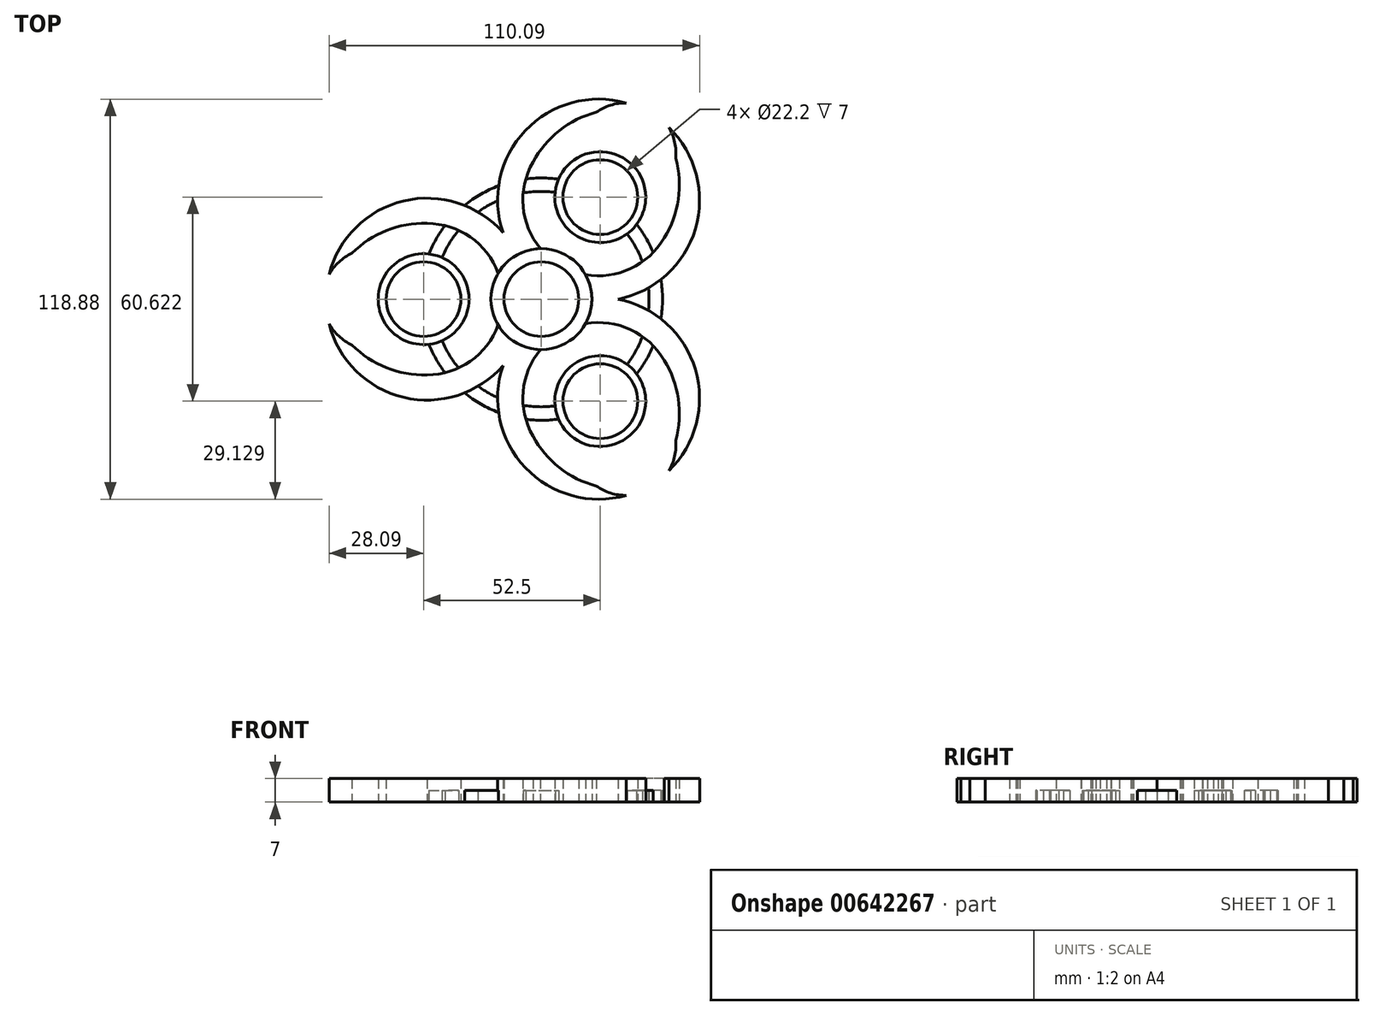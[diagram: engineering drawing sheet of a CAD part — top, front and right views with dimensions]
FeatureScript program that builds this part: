
annotation { "Feature Type Name" : "Feature", "Feature Type Description" : "" }
export const myFeature = defineFeature(function(context is Context, id is Id, definition is map)
    precondition{}
    {
        {
            var Q0;
            Q0=qCreatedBy(makeId("Top.planeOp"),FACE);
            var sketch = newSketch(context, id + "F0", { "sketchPlane" : qUnion([Q0])});
            skCircle(sketch, "E0", {"center": v(0, 0) * mm, "radius": 11.1 * mm});
            skCircle(sketch, "E1", {"center": v(0, 0) * mm, "radius": 15 * mm});
            skLineSegment(sketch, "E2", {"start": v(0, 0) * mm, "end": v(-35, 0) * mm, "construction": true});
            skCircle(sketch, "E3", {"center": v(-35, 0) * mm, "radius": 11.1 * mm});
            skCircle(sketch, "E4", {"center": v(-35, 0) * mm, "radius": 13.5 * mm});
            skCircle(sketch, "E5.1.0", {"center": v(17.5, -30.31) * mm, "radius": 11.1 * mm});
            skCircle(sketch, "E5.1.1", {"center": v(17.5, -30.31) * mm, "radius": 13.5 * mm});
            skCircle(sketch, "E5.2.0", {"center": v(17.5, 30.31) * mm, "radius": 11.1 * mm});
            skCircle(sketch, "E5.2.1", {"center": v(17.5, 30.31) * mm, "radius": 13.5 * mm});
            skSolve(sketch);
        }
        {
            var Q0;
            Q0=qCreatedBy(makeId("Top.planeOp"),FACE);
            var sketch = newSketch(context, id + "F1", { "sketchPlane" : qUnion([Q0])});
            skLineSegment(sketch, "E6", {"start": v(0, 0) * mm, "end": v(-34, 0) * mm, "construction": true});
            skArc(sketch, "E7", {"start": v(-34, -22.5) * mm, "mid": v(-11.5, 0) * mm, "end": v(-34, 22.5) * mm});
            skCircle(sketch, "E8", {"center": v(-34, 0) * mm, "radius": 30 * mm});
            skLineSegment(sketch, "E9", {"start": v(-34, 0) * mm, "end": v(-34, 30) * mm, "construction": true});
            skLineSegment(sketch, "E10", {"start": v(-34, 0) * mm, "end": v(-34, -30) * mm, "construction": true});
            skLineSegment(sketch, "E11", {"start": v(-34, 0) * mm, "end": v(-64, 0) * mm, "construction": true});
            skArc(sketch, "E12", {"start": v(-34, 22.5) * mm, "mid": v(-52.95, 16.52) * mm, "end": v(-64, 0) * mm});
            skArc(sketch, "E13.MirrorCS", {"start": v(-34, -22.5) * mm, "mid": v(-52.95, -16.52) * mm, "end": v(-64, 0) * mm});
            skPoint(sketch, "E14.center", {"position": v(0, 0) * mm});
            skCircle(sketch, "E15.0.0", {"center": v(0, 0) * mm, "radius": 15 * mm});
            skCircle(sketch, "E16.0.0", {"center": v(-35, 0) * mm, "radius": 13.5 * mm, "construction": true});
            skCircle(sketch, "E17.0.0", {"center": v(17.5, 30.31) * mm, "radius": 13.5 * mm, "construction": true});
            skCircle(sketch, "E18.0.0", {"center": v(17.5, -30.31) * mm, "radius": 13.5 * mm, "construction": true});
            skCircle(sketch, "E19.0", {"center": v(0, 0) * mm, "radius": 11.1 * mm});
            skCircle(sketch, "E20", {"center": v(-50, 0) * mm, "radius": 15 * mm});
            skArc(sketch, "E21.1.0", {"start": v(36.49, -18.2) * mm, "mid": v(5.75, -9.96) * mm, "end": v(-2.49, -40.7) * mm});
            skArc(sketch, "E21.1.1", {"start": v(36.49, -18.2) * mm, "mid": v(40.78, -37.6) * mm, "end": v(32, -55.43) * mm});
            skArc(sketch, "E21.1.2", {"start": v(-2.49, -40.7) * mm, "mid": v(12.17, -54.11) * mm, "end": v(32, -55.43) * mm});
            skCircle(sketch, "E21.1.3", {"center": v(17, -29.44) * mm, "radius": 30 * mm});
            skCircle(sketch, "E21.1.4", {"center": v(25, -43.3) * mm, "radius": 15 * mm});
            skArc(sketch, "E21.2.0", {"start": v(-2.49, 40.7) * mm, "mid": v(5.75, 9.96) * mm, "end": v(36.49, 18.2) * mm});
            skArc(sketch, "E21.2.1", {"start": v(-2.49, 40.7) * mm, "mid": v(12.17, 54.11) * mm, "end": v(32, 55.43) * mm});
            skArc(sketch, "E21.2.2", {"start": v(36.49, 18.2) * mm, "mid": v(40.78, 37.6) * mm, "end": v(32, 55.43) * mm});
            skCircle(sketch, "E21.2.3", {"center": v(17, 29.44) * mm, "radius": 30 * mm});
            skCircle(sketch, "E21.2.4", {"center": v(25, 43.3) * mm, "radius": 15 * mm});
            skSolve(sketch);
        }
        {
            var Q0;
            Q0=makeQuery(id+"F0.imprint","IMPRINT",FACE,{"disambiguationData":[TD([[makeQuery(id+"F0.imprint","IMPRINT",EDGE,{"derivedFrom":sQuery(id+"F0.wireOp",EDGE,"E0")}),-1.0]])]});
            var Q1;
            {var subQ0=sQuery(id+"F1.wireOp",EDGE,"E12");var subQ1=sQuery(id+"F1.wireOp",EDGE,"E7");var subQ2=makeQuery(id+"F1.imprint","INTERSECT",VERTEX,{"derivedFrom":[subQ1,subQ0]});Q1=makeQuery(id+"F1.imprint","IMPRINT",FACE,{"disambiguationData":[TD([[makeQuery(id+"F1.imprint","IMPRINT",EDGE,{"disambiguationData":[TD([[subQ2,1.0]])],"derivedFrom":subQ1}),-1.0]])]});}
            var Q2;
            {var subQ7=sQuery(id+"F1.wireOp",EDGE,"E8");var subQ9=sQuery(id+"F1.wireOp",EDGE,"E21.2.3");var subQ10=makeQuery(id+"F1.imprint","INTERSECT",VERTEX,{"disambiguationData":[OD(0.0)],"derivedFrom":[subQ7,subQ9]});Q2=makeQuery(id+"F1.imprint","IMPRINT",FACE,{"disambiguationData":[TD([[makeQuery(id+"F1.imprint","IMPRINT",EDGE,{"disambiguationData":[TD([[subQ10,1.0]])],"derivedFrom":subQ7}),-1.0]])]});}
            var Q3;
            {var subQ1=sQuery(id+"F1.wireOp",EDGE,"E21.2.0");var subQ5=sQuery(id+"F1.wireOp",EDGE,"E15.0.0");var subQ6=makeQuery(id+"F1.imprint","INTERSECT",VERTEX,{"disambiguationData":[OD(0.0)],"derivedFrom":[subQ5,subQ1]});Q3=makeQuery(id+"F1.imprint","IMPRINT",FACE,{"disambiguationData":[TD([[makeQuery(id+"F1.imprint","IMPRINT",EDGE,{"disambiguationData":[TD([[subQ6,1.0]])],"derivedFrom":subQ5}),-1.0]])]});}
            var Q4;
            {var subQ1=sQuery(id+"F1.wireOp",EDGE,"E21.1.0");var subQ3=sQuery(id+"F1.wireOp",EDGE,"E15.0.0");var subQ4=makeQuery(id+"F1.imprint","INTERSECT",VERTEX,{"disambiguationData":[OD(1.0)],"derivedFrom":[subQ3,subQ1]});Q4=makeQuery(id+"F1.imprint","IMPRINT",FACE,{"disambiguationData":[TD([[makeQuery(id+"F1.imprint","IMPRINT",EDGE,{"disambiguationData":[TD([[subQ4,-1.0]])],"derivedFrom":subQ3}),-1.0]])]});}
            var Q5;
            {var subQ0=sQuery(id+"F1.wireOp",EDGE,"E13.MirrorCS");var subQ1=sQuery(id+"F1.wireOp",EDGE,"E7");var subQ2=makeQuery(id+"F1.imprint","INTERSECT",VERTEX,{"derivedFrom":[subQ1,subQ0]});Q5=makeQuery(id+"F1.imprint","IMPRINT",FACE,{"disambiguationData":[TD([[makeQuery(id+"F1.imprint","IMPRINT",EDGE,{"disambiguationData":[TD([[subQ2,-1.0]])],"derivedFrom":subQ1}),-1.0]])]});}
            var Q6;
            {var subQ0=sQuery(id+"F1.wireOp",EDGE,"E21.2.3");var subQ1=sQuery(id+"F1.wireOp",EDGE,"E8");var subQ2=makeQuery(id+"F1.imprint","INTERSECT",VERTEX,{"disambiguationData":[OD(0.0)],"derivedFrom":[subQ1,subQ0]});Q6=makeQuery(id+"F1.imprint","IMPRINT",FACE,{"disambiguationData":[TD([[makeQuery(id+"F1.imprint","IMPRINT",EDGE,{"disambiguationData":[TD([[subQ2,1.0]])],"derivedFrom":subQ1}),1.0]])]});}
            var Q7;
            {var subQ0=sQuery(id+"F1.wireOp",EDGE,"E21.1.3");var subQ1=sQuery(id+"F1.wireOp",EDGE,"E15.0.0");var subQ2=makeQuery(id+"F1.imprint","INTERSECT",VERTEX,{"disambiguationData":[OD(0.0)],"derivedFrom":[subQ1,subQ0]});Q7=makeQuery(id+"F1.imprint","IMPRINT",FACE,{"disambiguationData":[TD([[makeQuery(id+"F1.imprint","IMPRINT",EDGE,{"disambiguationData":[TD([[subQ2,1.0]])],"derivedFrom":subQ1}),-1.0]])]});}
            var Q8;
            {var subQ5=sQuery(id+"F1.wireOp",EDGE,"E8");var subQ9=sQuery(id+"F1.wireOp",EDGE,"E21.1.3");var subQ10=makeQuery(id+"F1.imprint","INTERSECT",VERTEX,{"disambiguationData":[OD(0.0)],"derivedFrom":[subQ5,subQ9]});Q8=makeQuery(id+"F1.imprint","IMPRINT",FACE,{"disambiguationData":[TD([[makeQuery(id+"F1.imprint","IMPRINT",EDGE,{"disambiguationData":[TD([[subQ10,-1.0]])],"derivedFrom":subQ5}),-1.0]])]});}
            var Q9;
            {var subQ0=sQuery(id+"F1.wireOp",EDGE,"E21.1.3");var subQ1=sQuery(id+"F1.wireOp",EDGE,"E8");var subQ2=makeQuery(id+"F1.imprint","INTERSECT",VERTEX,{"disambiguationData":[OD(0.0)],"derivedFrom":[subQ1,subQ0]});Q9=makeQuery(id+"F1.imprint","IMPRINT",FACE,{"disambiguationData":[TD([[makeQuery(id+"F1.imprint","IMPRINT",EDGE,{"disambiguationData":[TD([[subQ2,-1.0]])],"derivedFrom":subQ1}),1.0]])]});}
            extrude(context, id + "F2", {"entities" : qUnion([Q0, Q1, Q2, Q3, Q4, Q5, Q6, Q7, Q8, Q9]), "depth" : 7 * mm, "offsetDistance" : 25 * mm});
        }
        {
            var Q0;
            Q0=makeQuery(id+"F0.imprint","IMPRINT",FACE,{"disambiguationData":[TD([[makeQuery(id+"F0.imprint","IMPRINT",EDGE,{"derivedFrom":sQuery(id+"F0.wireOp",EDGE,"E3")}),-1.0]])]});
            var Q1;
            Q1=makeQuery(id+"F0.imprint","IMPRINT",FACE,{"disambiguationData":[TD([[makeQuery(id+"F0.imprint","IMPRINT",EDGE,{"derivedFrom":sQuery(id+"F0.wireOp",EDGE,"E5.2.0")}),-1.0]])]});
            var Q2;
            Q2=makeQuery(id+"F0.imprint","IMPRINT",FACE,{"disambiguationData":[TD([[makeQuery(id+"F0.imprint","IMPRINT",EDGE,{"derivedFrom":sQuery(id+"F0.wireOp",EDGE,"E5.1.0")}),-1.0]])]});
            extrude(context, id + "F3", {"entities" : qUnion([Q0, Q1, Q2]), "operationType" : NewBodyOperationType.ADD, "depth" : 7 * mm, "offsetDistance" : 25 * mm});
        }
        {
            var Q0;
            Q0=qCreatedBy(makeId("Top.planeOp"),FACE);
            var sketch = newSketch(context, id + "F4", { "sketchPlane" : qUnion([Q0])});
            skArc(sketch, "E22.0", {"start": v(-34, -22.5) * mm, "mid": v(-11.5, 0) * mm, "end": v(-34, 22.5) * mm, "construction": true});
            skArc(sketch, "E23.0", {"start": v(-2.49, 40.7) * mm, "mid": v(5.75, 9.96) * mm, "end": v(36.49, 18.2) * mm, "construction": true});
            skArc(sketch, "E24.0", {"start": v(36.49, -18.2) * mm, "mid": v(5.75, -9.96) * mm, "end": v(-2.49, -40.7) * mm, "construction": true});
            skCircle(sketch, "E25", {"center": v(0, 0) * mm, "radius": 34 * mm, "construction": true});
            skArc(sketch, "E26.0", {"start": v(-33.41, -13.4) * mm, "mid": v(-31.3, -17.79) * mm, "end": v(-28.61, -21.85) * mm});
            skArc(sketch, "E27.0", {"start": v(-29.53, -12.34) * mm, "mid": v(-19.93, -25.04) * mm, "end": v(-5.4, -31.54) * mm});
            skCircle(sketch, "E28.0", {"center": v(-35, 0) * mm, "radius": 13.5 * mm, "construction": true});
            skCircle(sketch, "E29.0", {"center": v(17.5, -30.31) * mm, "radius": 13.5 * mm, "construction": true});
            skCircle(sketch, "E30.0", {"center": v(17.5, 30.31) * mm, "radius": 13.5 * mm, "construction": true});
            skArc(sketch, "E31.trimOffspring", {"start": v(4.08, 31.74) * mm, "mid": v(-0.67, 32) * mm, "end": v(-5.4, 31.54) * mm});
            skArc(sketch, "E32.trimOffspring", {"start": v(5.1, 35.64) * mm, "mid": v(0.24, 36) * mm, "end": v(-4.61, 35.7) * mm});
            skArc(sketch, "E33.trimOffspring", {"start": v(25.45, -19.4) * mm, "mid": v(28.04, -15.42) * mm, "end": v(30.02, -11.1) * mm});
            skArc(sketch, "E34.trimOffspring", {"start": v(28.32, -22.23) * mm, "mid": v(31.05, -18.21) * mm, "end": v(33.23, -13.86) * mm});
            skArc(sketch, "E35.0.0", {"start": v(-12.86, -7.71) * mm, "mid": v(-15, 0) * mm, "end": v(-12.86, 7.71) * mm, "construction": true});
            skArc(sketch, "E35.0.1", {"start": v(-12.86, 7.71) * mm, "mid": v(-21.1, 18.44) * mm, "end": v(-34, 22.5) * mm, "construction": true});
            skArc(sketch, "E35.0.2", {"start": v(-34, 22.5) * mm, "mid": v(-46.05, 20.38) * mm, "end": v(-56.26, 13.63) * mm, "construction": true});
            skArc(sketch, "E35.0.3", {"start": v(-56.26, 13.63) * mm, "mid": v(-35, 0) * mm, "end": v(-56.26, -13.63) * mm, "construction": true});
            skArc(sketch, "E35.0.4", {"start": v(-56.26, -13.63) * mm, "mid": v(-46.05, -20.38) * mm, "end": v(-34, -22.5) * mm, "construction": true});
            skArc(sketch, "E35.0.5", {"start": v(-34, -22.5) * mm, "mid": v(-21.1, -18.44) * mm, "end": v(-12.86, -7.71) * mm, "construction": true});
            skArc(sketch, "E36.0.0", {"start": v(-0.25, 15) * mm, "mid": v(7.5, 13) * mm, "end": v(13.11, 7.28) * mm, "construction": true});
            skArc(sketch, "E36.0.1", {"start": v(13.11, 7.28) * mm, "mid": v(26.52, 9.06) * mm, "end": v(36.49, 18.2) * mm, "construction": true});
            skArc(sketch, "E36.0.2", {"start": v(36.49, 18.2) * mm, "mid": v(40.68, 29.7) * mm, "end": v(39.93, 41.9) * mm, "construction": true});
            skArc(sketch, "E36.0.3", {"start": v(39.93, 41.9) * mm, "mid": v(17.5, 30.31) * mm, "end": v(16.32, 55.54) * mm, "construction": true});
            skArc(sketch, "E36.0.4", {"start": v(16.32, 55.54) * mm, "mid": v(5.37, 50.07) * mm, "end": v(-2.49, 40.7) * mm, "construction": true});
            skArc(sketch, "E36.0.5", {"start": v(-2.49, 40.7) * mm, "mid": v(-5.42, 27.5) * mm, "end": v(-0.25, 15) * mm, "construction": true});
            skArc(sketch, "E37.0.0", {"start": v(13.11, -7.28) * mm, "mid": v(7.5, -13) * mm, "end": v(-0.25, -15) * mm, "construction": true});
            skArc(sketch, "E37.0.1", {"start": v(-0.25, -15) * mm, "mid": v(-5.42, -27.5) * mm, "end": v(-2.49, -40.7) * mm, "construction": true});
            skArc(sketch, "E37.0.2", {"start": v(-2.49, -40.7) * mm, "mid": v(5.37, -50.07) * mm, "end": v(16.32, -55.54) * mm, "construction": true});
            skArc(sketch, "E37.0.3", {"start": v(16.32, -55.54) * mm, "mid": v(17.5, -30.31) * mm, "end": v(39.93, -41.9) * mm, "construction": true});
            skArc(sketch, "E37.0.4", {"start": v(39.93, -41.9) * mm, "mid": v(40.68, -29.7) * mm, "end": v(36.49, -18.2) * mm, "construction": true});
            skArc(sketch, "E37.0.5", {"start": v(36.49, -18.2) * mm, "mid": v(26.52, -9.06) * mm, "end": v(13.11, -7.28) * mm, "construction": true});
            skArc(sketch, "E38.trimOffspring", {"start": v(-4.61, 35.7) * mm, "mid": v(-22.04, 28.47) * mm, "end": v(-33.41, 13.4) * mm});
            skArc(sketch, "E39.trimOffspring", {"start": v(-5.4, 31.54) * mm, "mid": v(-19.93, 25.04) * mm, "end": v(-29.53, 12.34) * mm});
            skArc(sketch, "E40.trimOffspring", {"start": v(30.02, -11.1) * mm, "mid": v(31.65, 4.74) * mm, "end": v(25.45, 19.4) * mm});
            skArc(sketch, "E41.trimOffspring", {"start": v(33.23, -13.86) * mm, "mid": v(35.67, 4.85) * mm, "end": v(28.32, 22.23) * mm});
            skArc(sketch, "E42.trimOffspring", {"start": v(-5.4, -31.54) * mm, "mid": v(-0.67, -32) * mm, "end": v(4.08, -31.74) * mm});
            skArc(sketch, "E43.trimOffspring", {"start": v(-28.61, -21.85) * mm, "mid": v(-13.63, -33.32) * mm, "end": v(5.1, -35.64) * mm});
            skArc(sketch, "E44.0.0", {"start": v(-12.86, -7.71) * mm, "mid": v(-15, 0) * mm, "end": v(-12.86, 7.71) * mm});
            skArc(sketch, "E44.0.1", {"start": v(-12.86, 7.71) * mm, "mid": v(-21.1, 18.44) * mm, "end": v(-34, 22.5) * mm});
            skArc(sketch, "E44.0.2", {"start": v(-34, 22.5) * mm, "mid": v(-46.05, 20.38) * mm, "end": v(-56.26, 13.63) * mm});
            skArc(sketch, "E44.0.3", {"start": v(-56.26, 13.63) * mm, "mid": v(-35, 0) * mm, "end": v(-56.26, -13.63) * mm});
            skArc(sketch, "E44.0.4", {"start": v(-56.26, -13.63) * mm, "mid": v(-46.05, -20.38) * mm, "end": v(-34, -22.5) * mm});
            skArc(sketch, "E44.0.5", {"start": v(-34, -22.5) * mm, "mid": v(-21.1, -18.44) * mm, "end": v(-12.86, -7.71) * mm});
            skArc(sketch, "E45.0.0", {"start": v(-0.25, 15) * mm, "mid": v(7.5, 13) * mm, "end": v(13.11, 7.28) * mm});
            skArc(sketch, "E45.0.1", {"start": v(13.11, 7.28) * mm, "mid": v(26.52, 9.06) * mm, "end": v(36.49, 18.2) * mm});
            skArc(sketch, "E45.0.2", {"start": v(36.49, 18.2) * mm, "mid": v(40.68, 29.7) * mm, "end": v(39.93, 41.9) * mm});
            skArc(sketch, "E45.0.3", {"start": v(39.93, 41.9) * mm, "mid": v(17.5, 30.31) * mm, "end": v(16.32, 55.54) * mm});
            skArc(sketch, "E45.0.4", {"start": v(16.32, 55.54) * mm, "mid": v(5.37, 50.07) * mm, "end": v(-2.49, 40.7) * mm});
            skArc(sketch, "E45.0.5", {"start": v(-2.49, 40.7) * mm, "mid": v(-5.42, 27.5) * mm, "end": v(-0.25, 15) * mm});
            skArc(sketch, "E46.0.0", {"start": v(13.11, -7.28) * mm, "mid": v(7.5, -13) * mm, "end": v(-0.25, -15) * mm});
            skArc(sketch, "E46.0.1", {"start": v(-0.25, -15) * mm, "mid": v(-5.42, -27.5) * mm, "end": v(-2.49, -40.7) * mm});
            skArc(sketch, "E46.0.2", {"start": v(-2.49, -40.7) * mm, "mid": v(5.37, -50.07) * mm, "end": v(16.32, -55.54) * mm});
            skArc(sketch, "E46.0.3", {"start": v(16.32, -55.54) * mm, "mid": v(17.5, -30.31) * mm, "end": v(39.93, -41.9) * mm});
            skArc(sketch, "E46.0.4", {"start": v(39.93, -41.9) * mm, "mid": v(40.68, -29.7) * mm, "end": v(36.49, -18.2) * mm});
            skArc(sketch, "E46.0.5", {"start": v(36.49, -18.2) * mm, "mid": v(26.52, -9.06) * mm, "end": v(13.11, -7.28) * mm});
            skCircle(sketch, "E47.0.0", {"center": v(-35, 0) * mm, "radius": 13.5 * mm});
            skCircle(sketch, "E48.0.0", {"center": v(17.5, 30.31) * mm, "radius": 13.5 * mm});
            skCircle(sketch, "E49.0.0", {"center": v(17.5, -30.31) * mm, "radius": 13.5 * mm});
            skSolve(sketch);
        }
        {
            var Q0;
            {var subQ0=sQuery(id+"F4.wireOp",EDGE,"E38.trimOffspring");Q0=makeQuery(id+"F4.imprint","IMPRINT",FACE,{"disambiguationData":[TD([[makeQuery(id+"F4.imprint","IMPRINT",EDGE,{"derivedFrom":subQ0}),1.0]])]});}
            var Q1;
            {var subQ0=sQuery(id+"F4.wireOp",EDGE,"E26.0");Q1=makeQuery(id+"F4.imprint","IMPRINT",FACE,{"disambiguationData":[TD([[makeQuery(id+"F4.imprint","IMPRINT",EDGE,{"derivedFrom":subQ0}),1.0]])]});}
            var Q2;
            {var subQ0=sQuery(id+"F4.wireOp",EDGE,"E42.trimOffspring");Q2=makeQuery(id+"F4.imprint","IMPRINT",FACE,{"disambiguationData":[TD([[makeQuery(id+"F4.imprint","IMPRINT",EDGE,{"derivedFrom":subQ0}),-1.0]])]});}
            var Q3;
            {var subQ0=sQuery(id+"F4.wireOp",EDGE,"E33.trimOffspring");Q3=makeQuery(id+"F4.imprint","IMPRINT",FACE,{"disambiguationData":[TD([[makeQuery(id+"F4.imprint","IMPRINT",EDGE,{"derivedFrom":subQ0}),-1.0]])]});}
            var Q4;
            {var subQ0=sQuery(id+"F4.wireOp",EDGE,"E40.trimOffspring");Q4=makeQuery(id+"F4.imprint","IMPRINT",FACE,{"disambiguationData":[TD([[makeQuery(id+"F4.imprint","IMPRINT",EDGE,{"derivedFrom":subQ0}),-1.0]])]});}
            var Q5;
            {var subQ0=sQuery(id+"F4.wireOp",EDGE,"E31.trimOffspring");Q5=makeQuery(id+"F4.imprint","IMPRINT",FACE,{"disambiguationData":[TD([[makeQuery(id+"F4.imprint","IMPRINT",EDGE,{"derivedFrom":subQ0}),-1.0]])]});}
            var Q6;
            {var subQ1=sQuery(id+"F4.wireOp",EDGE,"E27.0");var subQ3=sQuery(id+"F4.wireOp",EDGE,"E44.0.5");var subQ4=makeQuery(id+"F4.imprint","INTERSECT",VERTEX,{"derivedFrom":[subQ1,subQ3]});Q6=makeQuery(id+"F4.imprint","IMPRINT",FACE,{"disambiguationData":[TD([[makeQuery(id+"F4.imprint","IMPRINT",EDGE,{"disambiguationData":[TD([[subQ4,-1.0]])],"derivedFrom":subQ1}),-1.0]])]});}
            extrude(context, id + "F5", {"entities" : qUnion([Q0, Q1, Q2, Q3, Q4, Q5, Q6]), "operationType" : NewBodyOperationType.ADD, "depth" : 3.5 * mm, "offsetDistance" : 25 * mm});
        }
    });
